# Revit family: 雨、污水检查井 - 土建2016
name_source: partatom
category: 管道附件
revit_build: Autodesk Revit 2016 (Build: 20150212_1515(x64)
units: mm (PartAtom-declared; Revit-internal decimal feet)

## family parameters
共享 = 否
加载时剪切的空心 = 否
圆形连接件大小 = 使用直径
基于工作平面 = 否
总是垂直 = 是
零件类型 = 标准

## types (2) — shared parameters
URL = www.goujianwu.com
井基 = 混凝土
井基半径 = 790  [stored 2.59186 ft]
井基厚度 = 150
井基直径 = 1580  [stored 5.18373 ft]
井墙 = 水泥砂浆砌砖
井壁厚 = 240  [stored 0.787402 ft]
井盖 = 水泥砂浆
井盖半径 = 400  [stored 1.31234 ft]
井盖厚度 = 100  [stored 0.328084 ft]
井盖直径 = 800  [stored 2.62467 ft]
井筒内半径 = 350  [stored 1.14829 ft]
井筒内径 = 700
井筒外半径 = 590  [stored 1.9357 ft]
井身外半径 = 740  [stored 2.42782 ft]
井身高度 = 1800  [stored 5.90551 ft]
座浆 = 水泥砂浆
座浆厚度 = 100  [stored 0.328084 ft]
座浆外半径 = 690  [stored 2.26378 ft]
检查井半径 = 500  [stored 1.64042 ft]
直径 = 1000  [stored 3.28084 ft]
说明 = 永久免费族库下载，找构件就上构件坞

## type names (no varying parameters)
- 1000x3800
- 污水井

note: [stored X ft] marks values corroborated as IEEE doubles in the binary element streams (Revit-internal decimal feet)
